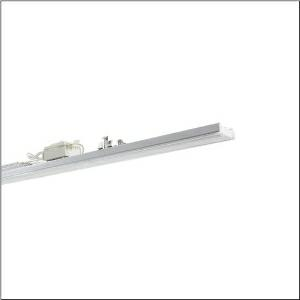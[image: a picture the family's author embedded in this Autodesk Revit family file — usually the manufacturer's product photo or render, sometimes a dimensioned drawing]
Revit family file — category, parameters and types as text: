
# Revit family: licross_r__11_recessed_mo_51te19mn495g_12e7
name_source: partatom
category: Lighting Fixtures
units: mm (PartAtom-declared; Revit-internal decimal feet)

## family parameters
Cut with Voids When Loaded = No
Host = Face
Light Source = No
Part Type = Normal
Room Calculation Point = No
Round Connector Dimension = Use Diameter
Shared = No

## types (1)
- --- (1 x LED, 9850 lm, 55.2 W, 4000K)
    Apparent Load = 55 VA
    CIE Flux Codes = 55 90 98 100 100
    Color Rendering = 80
    Color Temperature = 4000K
    Default Elevation = 1800 mm
    Description = Licross® 11 Recessed MO, luminaire insert, of sheet steel, galvanised, coil coated, white, length: 1.500mm, width: 66mm, height: 67mm, LED rated luminous flux: 9.860lm, light colour: 840, control gear: ON/OFF Multilumen, with plug, 3-pole, with phase selection, mains connection: 220..240V, AC, 50/60Hz, rated input power: 55W, internal wiring halogen-free, primary light control with lens, of plastic, primary optical cover: cover, of PMMA, light emission: direct distribution, primary light characteristic: double asymmetric, protection rating (complete): IP54, insulation class (complete): insulation class I (protective earthing), certification: CE, ENEC, VDE, UKCA, protection symbol: D if used in an environment with non-conductive dust loads with corresponding accessories, impact resistance: IK06, permissible ambient temperature for indoor applications: -35..+40°C, corresponds to IFS (International Featured Standards) requirements for safety and quality in the food industry, reducing of maximum allowable ambient temperature of 5°C with ceiling mounting, packaging unit: 1 piece
    Height = 58 mm
    Lamp = 1 x LED
    Lamp Light Flux = 9850 lm
    Lamp Power = 55.2 W
    Lamp count = 1
    Length = 1500 mm
    Luminous efficacy = 178 lm/W
    Manufacturer = Siteco
    ModVariant = No
    Model = 51TE19MN495G
    Mounting Place = Ceiling
    Mounting Type = Pendant
    Number of Poles = 1
    OnlyDefault = Yes
    Power Factor = 1
    Product Name = Licross® 11 Recessed MO
    Product group = luminaire insert | ceiling pendant
    ProductGroupID = 902
    Protection Class = Protection class I
    Protection Degree = IP 54
    RLX_Detail_Level = 1
    RLX_Emergency_Light_Flux = 0 lm
    RLX_Emergency_Type = 0
    RLX_Emergency_Type_DB = No
    RlxData = <blob elided: 22221 chars, md5=42f3df51>
    Socket = socket
    Standby Power = 0 W
    System Light Flux = 9850 lm
    System Power = 55 W
    Type Comments = factory setting: luminous flux: 100 % | (A | C | E) | 126 mA
    Type Image = l_1296930.jpg
    URL = http://relux.com
    VarID = @adj_107159
    Voltage = 0 V
    Weight = 0.00 kg
    Width = 66 mm

## geometry (parser evidence)
native form markers: Blend x4, Sweep x9
no freeform markers — native parametric forms only
